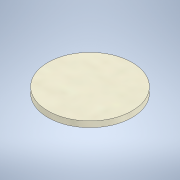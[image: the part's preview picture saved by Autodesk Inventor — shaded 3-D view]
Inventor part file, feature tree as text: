
AUTODESK INVENTOR PART (.ipt)
format: ipt  version: 2021 (Build 250183000, 183)  size: 96,768 bytes
history: native  units: mm
features: extrude x1, sketch x1
ambient origin geometry x8: Origin, YZ Plane, XZ Plane, XY Plane, X Axis, Y Axis, Z Axis, Center Point
bodies: Solid1 (feature_tree)
feature tree (2):
  extrude  "Extrusion1"  Depth=1.75mm TaperAngle=0.0deg
  sketch  "Sketch1"  dims[d0=25.25mm d1=1.75mm d2=0.0mm]
